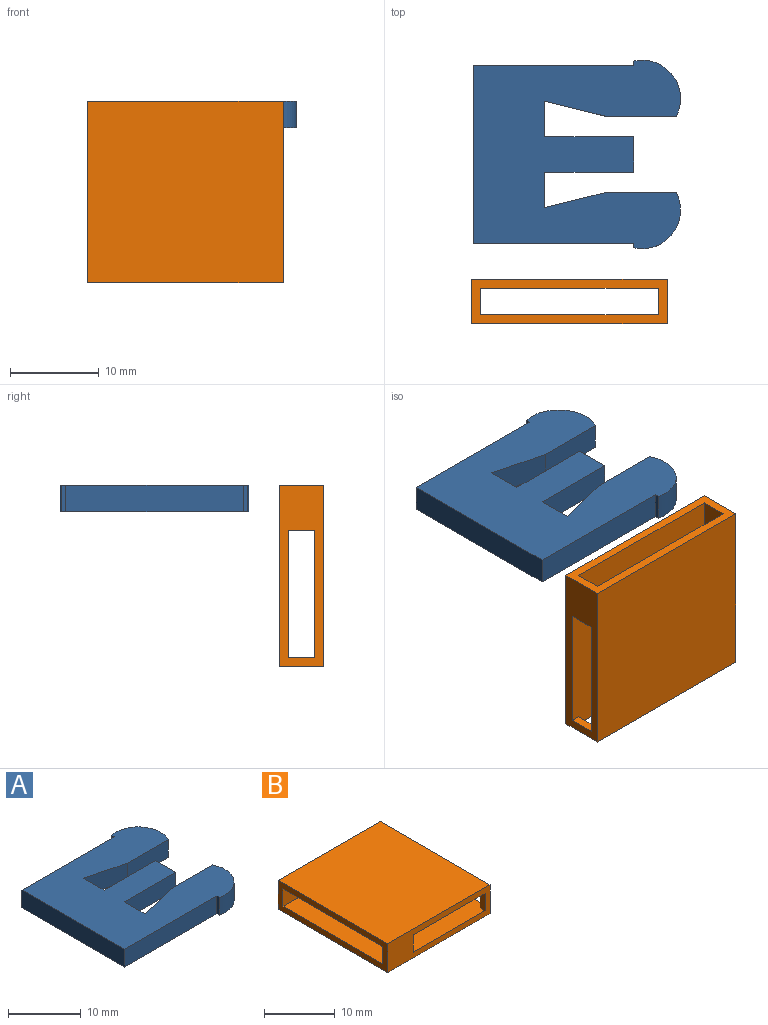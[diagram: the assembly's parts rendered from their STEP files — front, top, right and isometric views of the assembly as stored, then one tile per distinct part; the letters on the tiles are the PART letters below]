
ASSEMBLY  parts=2 mates=1
PART A: 18 faces, bbox 23.3x21.2x3 mm
  f0: plane 20x3mm, normal (-1,0,0), area 60mm2, adj f1,f15,f16,f17
  f1: plane 18x3mm, normal (0,-1,0), area 54mm2, adj f0,f2,f16,f17
  f2: plane 3x0.5mm, normal (-1,0,0), area 1.5mm2, adj f1,f3,f16,f17
  f3: cylinder r=4.33mm len=6.32mm, axis (0,0,-1), area 29.4mm2, adj f2,f4,f16,f17
  f4: plane 8x3mm, normal (0,1,0), area 24mm2, adj f3,f5,f16,f17
  f5: plane 6.79x3mm, normal (-0.24,0.97,0), area 21mm2, adj f4,f6,f16,f17
  f6: plane 4x3mm, normal (1,0,0), area 12mm2, adj f5,f7,f16,f17
  f7: plane 10x3mm, normal (0,-1,0), area 30mm2, adj f6,f8,f16,f17
  f8: plane 4x3mm, normal (1,0,0), area 12mm2, adj f7,f9,f16,f17
  f9: plane 10x3mm, normal (0,1,0), area 30mm2, adj f8,f10,f16,f17
  f10: plane 4x3mm, normal (1,0,0), area 12mm2, adj f9,f11,f16,f17
  f11: plane 6.79x3mm, normal (-0.24,-0.97,0), area 21mm2, adj f10,f12,f16,f17
  f12: plane 8x3mm, normal (0,-1,0), area 24mm2, adj f11,f13,f16,f17
  f13: cylinder r=4.33mm len=6.32mm, axis (0,0,-1), area 29.4mm2, adj f12,f14,f16,f17
  f14: plane 3x0.5mm, normal (-1,0,0), area 1.5mm2, adj f13,f15,f16,f17
  f15: plane 18x3mm, normal (0,1,0), area 54mm2, adj f0,f14,f16,f17
  f16: plane 23.27x21.21mm, normal (0,0,1), area 360.5mm2, adj f0,f1,f2,f3,f4,f5,f6,f7
  f17: plane 23.27x21.21mm, normal (0,0,-1), area 360.5mm2, adj f0,f1,f2,f3,f4,f5,f6,f7
PART B: 16 faces, bbox 20.4x22x5 mm
  f0: plane 20.43x5mm, normal (0,-1,0), area 59.2mm2, adj f4,f5,f6,f7,f8,f10,f14,f15
  f1: plane 20.43x5mm, normal (0,1,0), area 59.2mm2, adj f4,f5,f6,f7,f8,f10,f12,f13
  f2: plane 3x1mm, normal (0,1,0), area 3mm2, adj f5,f8,f10,f15
  f3: plane 3x1mm, normal (0,-1,0), area 3mm2, adj f5,f8,f10,f12
  f4: plane 22x5mm, normal (-1,0,0), area 50mm2, adj f0,f1,f6,f7,f8,f9,f10,f11
  f5: plane 22x5mm, normal (1,0,0), area 50mm2, adj f0,f1,f2,f3,f6,f7,f8,f10
  f6: plane 22x20.43mm, normal (0,0,1), area 449.5mm2, adj f0,f1,f4,f5
  f7: plane 22x20.43mm, normal (0,0,-1), area 449.5mm2, adj f0,f1,f4,f5
  f8: plane 22x20.43mm, normal (0,0,-1), area 437.3mm2, adj f0,f1,f2,f3,f4,f5,f9,f11
  f9: plane 5.1x3mm, normal (0,1,0), area 15.3mm2, adj f4,f8,f10,f14
  f10: plane 22x20.43mm, normal (0,0,1), area 437.3mm2, adj f0,f1,f2,f3,f4,f5,f9,f11
  f11: plane 5.1x3mm, normal (0,-1,0), area 15.3mm2, adj f4,f8,f10,f13
  f12: plane 3x1mm, normal (-1,0,0), area 3mm2, adj f1,f3,f8,f10
  f13: plane 3x1mm, normal (1,0,0), area 3mm2, adj f1,f8,f10,f11
  f14: plane 3x1mm, normal (1,0,0), area 3mm2, adj f0,f8,f9,f10
  f15: plane 3x1mm, normal (-1,0,0), area 3mm2, adj f0,f2,f8,f10
PLACE A t=(-10.88,5.6,-3.08)mm
PLACE B rot(axis=(-0.58,0.58,0.58),120deg) t=(-0.11,-12.43,12.82)mm
MATE planar B.f4 <-> A.f16  axis (0,0,1) through (9.89,-12.43,-0.08)mm
